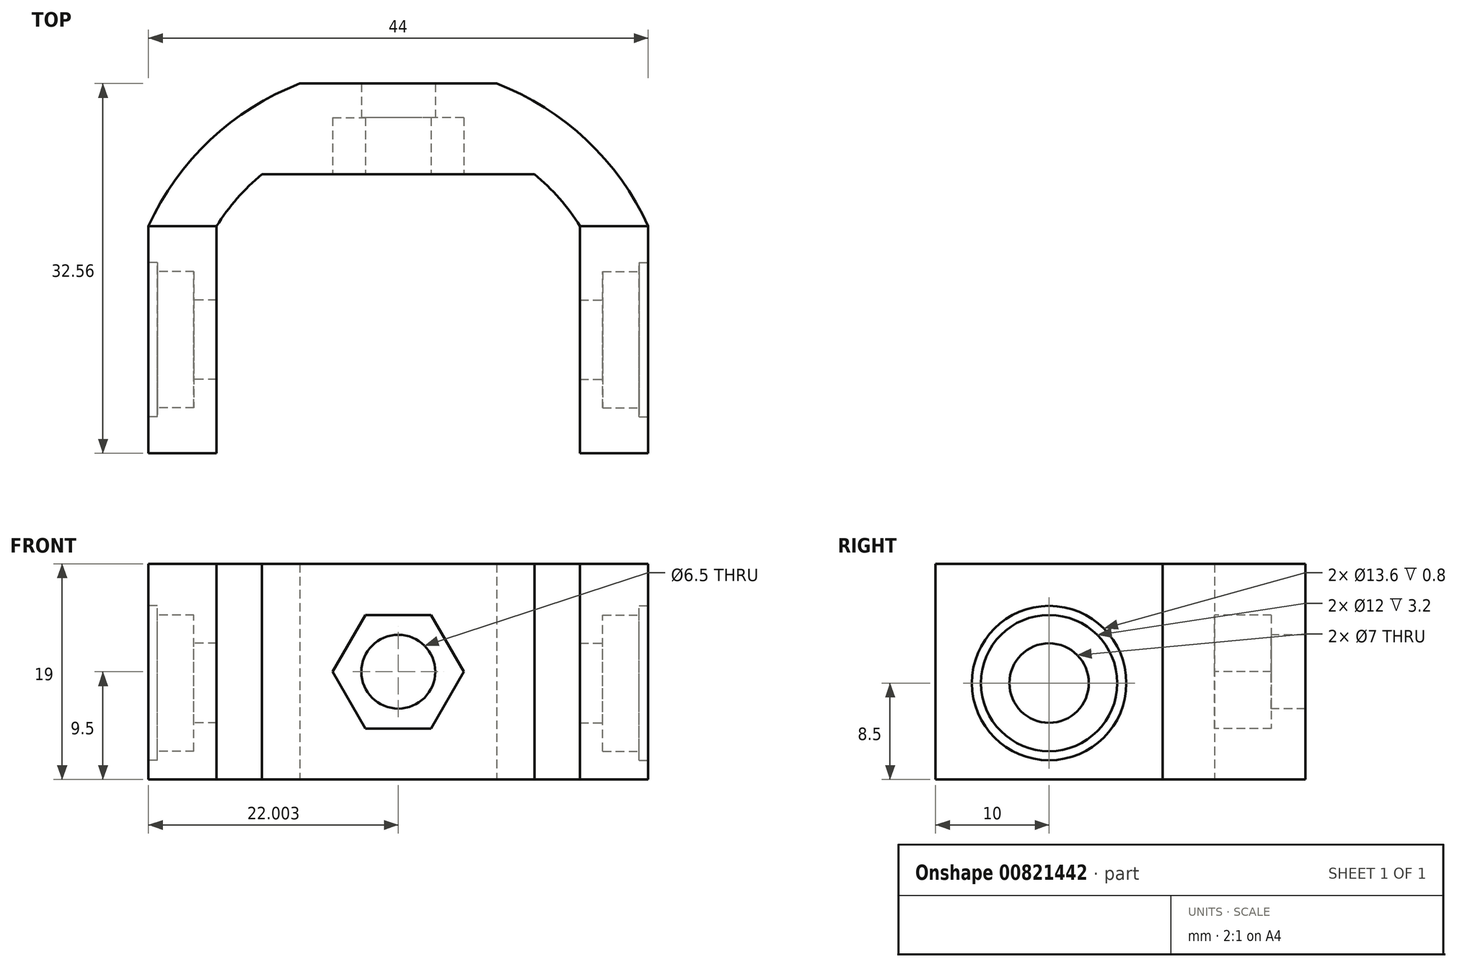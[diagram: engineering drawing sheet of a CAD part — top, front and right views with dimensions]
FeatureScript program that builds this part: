
annotation { "Feature Type Name" : "Feature", "Feature Type Description" : "" }
export const myFeature = defineFeature(function(context is Context, id is Id, definition is map)
    precondition{}
    {
        {
            var Q0;
            Q0=qCreatedBy(makeId("Right.planeOp"),FACE);
            var sketch = newSketch(context, id + "F0", { "sketchPlane" : qUnion([Q0])});
            skLineSegment(sketch, "E0.bottom", {"start": v(10, -9.5) * mm, "end": v(-10, -9.5) * mm});
            skLineSegment(sketch, "E0.top", {"start": v(10, 9.5) * mm, "end": v(-10, 9.5) * mm});
            skLineSegment(sketch, "E0.left", {"start": v(10, -9.5) * mm, "end": v(10, 9.5) * mm});
            skLineSegment(sketch, "E0.right", {"start": v(-10, -9.5) * mm, "end": v(-10, 9.5) * mm});
            skPoint(sketch, "E0.middle", {"position": v(0, 0) * mm});
            skSolve(sketch);
        }
        {
            var Q0;
            Q0 = qSketchRegion(id + "F0", true);
            extrude(context, id + "F1", {"entities" : qUnion([Q0]), "depth" : 6 * mm, "offsetDistance" : 25 * mm});
        }
        {
            var Q0;
            Q0=makeQuery(id+"F1.opExtrude","CAP_FACE",FACE,{"disambiguationData":[OSD([sQuery(id+"F0.wireOp",EDGE,"E0.bottom"),sQuery(id+"F0.wireOp",EDGE,"E0.top"),sQuery(id+"F0.wireOp",EDGE,"E0.left"),sQuery(id+"F0.wireOp",EDGE,"E0.right")])],"isStart":false});
            var sketch = newSketch(context, id + "F2", { "sketchPlane" : qUnion([Q0])});
            skCircle(sketch, "E1", {"center": v(0, -1) * mm, "radius": 6.8 * mm});
            skSolve(sketch);
        }
        {
            var Q0;
            Q0 = qSketchRegion(id + "F2", true);
            extrude(context, id + "F3", {"entities" : qUnion([Q0]), "operationType" : NewBodyOperationType.REMOVE, "oppositeDirection" : true, "depth" : 0.8 * mm, "offsetDistance" : 25 * mm});
        }
        {
            var Q0;
            Q0=makeQuery(id+"F3.boolean.opBoolean","COPY",FACE,{"derivedFrom":makeQuery(id+"F3.opExtrude","CAP_FACE",FACE,{"disambiguationData":[OSD([sQuery(id+"F2.wireOp",EDGE,"E1")])],"isStart":false})});
            var sketch = newSketch(context, id + "F4", { "sketchPlane" : qUnion([Q0])});
            skCircle(sketch, "E2", {"center": v(0, -1) * mm, "radius": 6 * mm});
            skSolve(sketch);
        }
        {
            var Q0;
            Q0 = qSketchRegion(id + "F4", true);
            extrude(context, id + "F5", {"entities" : qUnion([Q0]), "operationType" : NewBodyOperationType.REMOVE, "oppositeDirection" : true, "depth" : 3.2 * mm, "offsetDistance" : 25 * mm});
        }
        {
            var Q0;
            Q0=makeQuery(id+"F5.boolean.opBoolean","COPY",FACE,{"derivedFrom":makeQuery(id+"F5.opExtrude","CAP_FACE",FACE,{"disambiguationData":[OSD([sQuery(id+"F4.wireOp",EDGE,"E2")])],"isStart":false})});
            var sketch = newSketch(context, id + "F6", { "sketchPlane" : qUnion([Q0])});
            skCircle(sketch, "E3", {"center": v(0, -1) * mm, "radius": 3.5 * mm});
            skSolve(sketch);
        }
        {
            var Q0;
            Q0 = qSketchRegion(id + "F6", true);
            extrude(context, id + "F7", {"entities" : qUnion([Q0]), "operationType" : NewBodyOperationType.REMOVE, "endBound" : BoundingType.UP_TO_NEXT, "oppositeDirection" : true, "depth" : 25 * mm, "offsetDistance" : 25 * mm});
        }
        {
            var Q0;
            Q0=qCreatedBy(makeId("Right.planeOp"),FACE);
            cPlane(context, id + "F8", {"entities" : qUnion([Q0]), "cplaneType" : CPlaneType.OFFSET, "offset" : 16 * mm, "oppositeDirection" : true, "width" : 150 * mm, "height" : 150 * mm});
        }
        {
            var Q0;
            Q0=makeQuery(id+"F1.opExtrude","SWEPT_BODY",BODY,{"disambiguationData":[OSD([sQuery(id+"F0.wireOp",EDGE,"E0.bottom"),sQuery(id+"F0.wireOp",EDGE,"E0.top"),sQuery(id+"F0.wireOp",EDGE,"E0.left"),sQuery(id+"F0.wireOp",EDGE,"E0.right")])]});
            var Q1;
            Q1=qCreatedBy(id+"F8.planeOp",FACE);
            mirror(context, id + "F9", {"entities" : qUnion([Q0]), "mirrorPlane" : qUnion([Q1])});
        }
        {
            var Q0;
            Q0=qCreatedBy(makeId("Top.planeOp"),FACE);
            var sketch = newSketch(context, id + "F10", { "sketchPlane" : qUnion([Q0])});
            skArc(sketch, "E4", {"start": v(0, 10) * mm, "mid": v(-16, 18.87) * mm, "end": v(-32, 10) * mm});
            skArc(sketch, "E5", {"start": v(6, 10) * mm, "mid": v(-16, 24.17) * mm, "end": v(-38, 10) * mm});
            skLineSegment(sketch, "E6", {"start": v(-38, 10) * mm, "end": v(-32, 10) * mm});
            skLineSegment(sketch, "E7", {"start": v(0, 10) * mm, "end": v(6, 10) * mm});
            skSolve(sketch);
        }
        {
            var Q0;
            Q0 = qSketchRegion(id + "F10", true);
            extrude(context, id + "F11", {"entities" : qUnion([Q0]), "endBound" : BoundingType.SYMMETRIC, "depth" : 19 * mm, "offsetDistance" : 25 * mm});
        }
        {
            var Q0;
            Q0=qCreatedBy(makeId("Top.planeOp"),FACE);
            var sketch = newSketch(context, id + "F12", { "sketchPlane" : qUnion([Q0])});
            skLineSegment(sketch, "E8.bottom", {"start": v(-28, 19.56) * mm, "end": v(-4, 19.56) * mm});
            skLineSegment(sketch, "E8.top", {"start": v(-28, 14.56) * mm, "end": v(-4, 14.56) * mm});
            skLineSegment(sketch, "E8.left", {"start": v(-28, 19.56) * mm, "end": v(-28, 14.56) * mm});
            skLineSegment(sketch, "E8.right", {"start": v(-4, 19.56) * mm, "end": v(-4, 14.56) * mm});
            skSolve(sketch);
        }
        {
            var Q0;
            Q0 = qSketchRegion(id + "F12", true);
            extrude(context, id + "F13", {"entities" : qUnion([Q0]), "operationType" : NewBodyOperationType.ADD, "endBound" : BoundingType.SYMMETRIC, "depth" : 19 * mm, "offsetDistance" : 25 * mm});
        }
        {
            var Q0;
            Q0=makeQuery(id+"F13.opExtrude","SWEPT_FACE",FACE,{"disambiguationData":[OSD([sQuery(id+"F12.wireOp",EDGE,"E8.top")])]});
            var sketch = newSketch(context, id + "F14", { "sketchPlane" : qUnion([Q0])});
            skCircle(sketch, "E9.cCircle", {"center": v(-16, 0) * mm, "radius": 5 * mm, "construction": true});
            skLineSegment(sketch, "E9.0", {"start": v(-13.11, -5) * mm, "end": v(-18.89, -5) * mm});
            skLineSegment(sketch, "E9.1", {"start": v(-18.89, -5) * mm, "end": v(-21.77, 0) * mm});
            skLineSegment(sketch, "E9.2", {"start": v(-21.77, 0) * mm, "end": v(-18.89, 5) * mm});
            skLineSegment(sketch, "E9.3", {"start": v(-18.89, 5) * mm, "end": v(-13.11, 5) * mm});
            skLineSegment(sketch, "E9.4", {"start": v(-13.11, 5) * mm, "end": v(-10.23, 0) * mm});
            skLineSegment(sketch, "E9.5", {"start": v(-10.23, 0) * mm, "end": v(-13.11, -5) * mm});
            skPoint(sketch, "E9.0.midPoint", {"position": v(-16, -5) * mm});
            skSolve(sketch);
        }
        {
            var Q0;
            Q0 = qSketchRegion(id + "F14", true);
            extrude(context, id + "F15", {"entities" : qUnion([Q0]), "operationType" : NewBodyOperationType.REMOVE, "oppositeDirection" : true, "depth" : 5 * mm, "offsetDistance" : 25 * mm});
        }
        {
            var Q0;
            Q0=makeQuery(id+"F15.boolean.opBoolean","COPY",FACE,{"derivedFrom":makeQuery(id+"F15.opExtrude","CAP_FACE",FACE,{"disambiguationData":[OSD([sQuery(id+"F14.wireOp",EDGE,"E9.0"),sQuery(id+"F14.wireOp",EDGE,"E9.1"),sQuery(id+"F14.wireOp",EDGE,"E9.2"),sQuery(id+"F14.wireOp",EDGE,"E9.3"),sQuery(id+"F14.wireOp",EDGE,"E9.4"),sQuery(id+"F14.wireOp",EDGE,"E9.5")])],"isStart":false})});
            var sketch = newSketch(context, id + "F16", { "sketchPlane" : qUnion([Q0])});
            skCircle(sketch, "E10", {"center": v(-16, 0) * mm, "radius": 3.25 * mm});
            skSolve(sketch);
        }
        {
            var Q0;
            Q0 = qSketchRegion(id + "F16", true);
            extrude(context, id + "F17", {"entities" : qUnion([Q0]), "operationType" : NewBodyOperationType.REMOVE, "oppositeDirection" : true, "depth" : 25 * mm, "offsetDistance" : 25 * mm});
        }
        {
            var Q0;
            Q0=qCreatedBy(makeId("Top.planeOp"),FACE);
            var sketch = newSketch(context, id + "F18", { "sketchPlane" : qUnion([Q0])});
            skLineSegment(sketch, "E11.bottom", {"start": v(-29, 27.56) * mm, "end": v(-3, 27.56) * mm});
            skLineSegment(sketch, "E11.top", {"start": v(-29, 22.56) * mm, "end": v(-3, 22.56) * mm});
            skLineSegment(sketch, "E11.left", {"start": v(-29, 27.56) * mm, "end": v(-29, 22.56) * mm});
            skLineSegment(sketch, "E11.right", {"start": v(-3, 27.56) * mm, "end": v(-3, 22.56) * mm});
            skSolve(sketch);
        }
        {
            var Q0;
            Q0 = qSketchRegion(id + "F18", true);
            extrude(context, id + "F19", {"entities" : qUnion([Q0]), "operationType" : NewBodyOperationType.REMOVE, "endBound" : BoundingType.SYMMETRIC, "oppositeDirection" : true, "depth" : 25 * mm, "offsetDistance" : 25 * mm});
        }
    });
